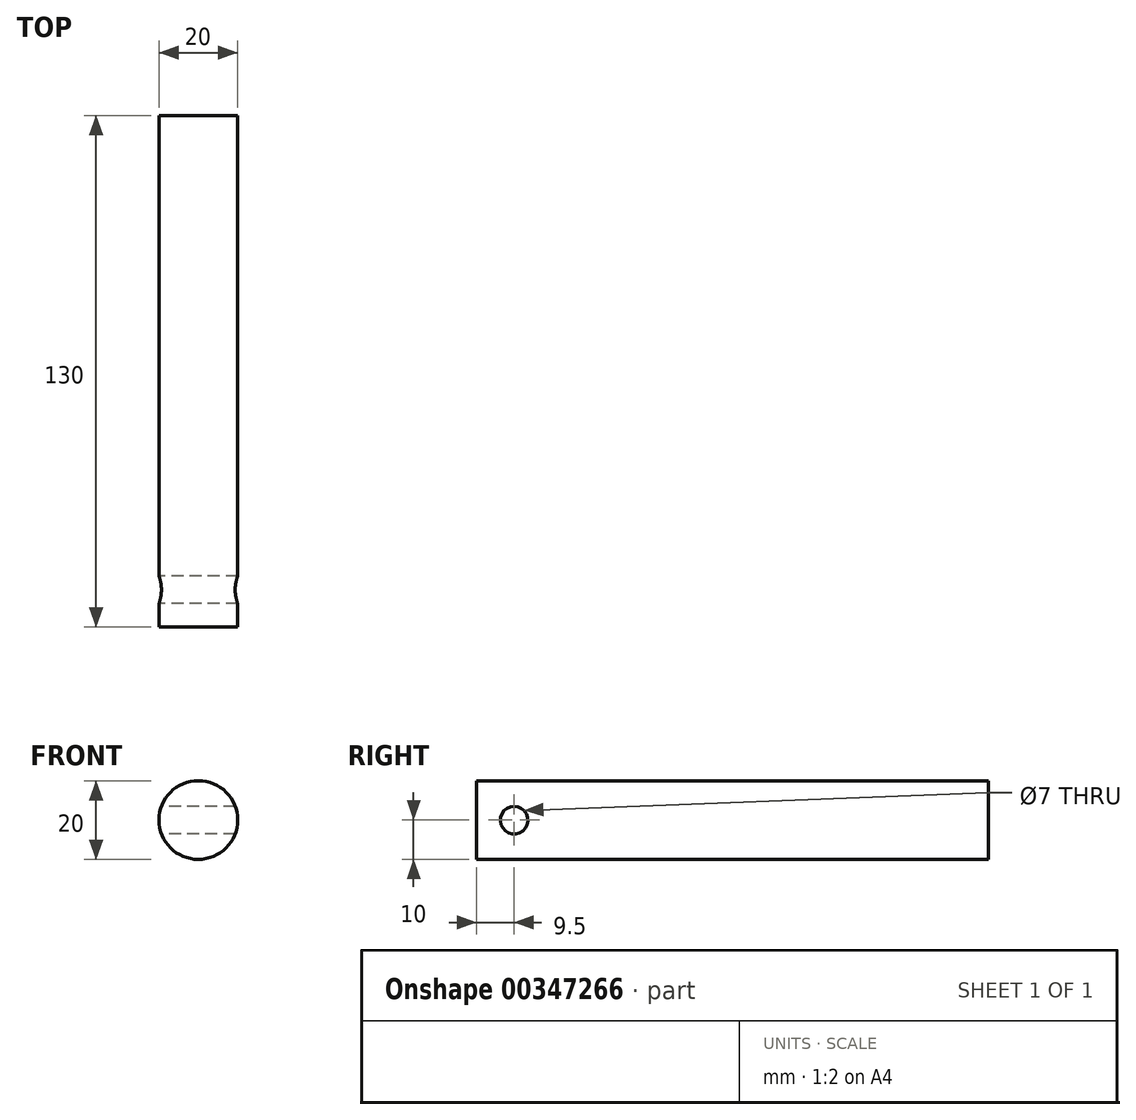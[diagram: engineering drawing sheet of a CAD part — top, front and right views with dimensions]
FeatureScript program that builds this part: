
annotation { "Feature Type Name" : "Feature", "Feature Type Description" : "" }
export const myFeature = defineFeature(function(context is Context, id is Id, definition is map)
    precondition{}
    {
        {
            var Q0;
            Q0=qCreatedBy(makeId("Front.planeOp"),FACE);
            var sketch = newSketch(context, id + "F0", { "sketchPlane" : qUnion([Q0])});
            skCircle(sketch, "E0", {"center": v(0, 0) * mm, "radius": 10 * mm});
            skSolve(sketch);
        }
        {
            var Q0;
            Q0=qCreatedBy(makeId("Right.planeOp"),FACE);
            var sketch = newSketch(context, id + "F1", { "sketchPlane" : qUnion([Q0])});
            skLineSegment(sketch, "E1.bottom", {"start": v(0, -10) * mm, "end": v(-130, -10) * mm});
            skLineSegment(sketch, "E1.top", {"start": v(0, 10) * mm, "end": v(-130, 10) * mm});
            skLineSegment(sketch, "E1.left", {"start": v(0, -10) * mm, "end": v(0, 10) * mm});
            skLineSegment(sketch, "E1.right", {"start": v(-130, -10) * mm, "end": v(-130, 10) * mm});
            skCircle(sketch, "E2", {"center": v(-120.5, 0) * mm, "radius": 3.5 * mm});
            skSolve(sketch);
        }
        {
            var Q0;
            Q0=makeQuery(id+"F1.imprint","IMPRINT",FACE,{"disambiguationData":[TD([[makeQuery(id+"F1.imprint","IMPRINT",EDGE,{"derivedFrom":sQuery(id+"F1.wireOp",EDGE,"E1.bottom")}),-1.0]])]});
            extrude(context, id + "F2", {"entities" : qUnion([Q0]), "depth" : 25 * mm, "symmetric" : true});
        }
        {
            var Q0;
            Q0 = qSketchRegion(id + "F0", true);
            extrude(context, id + "F3", {"entities" : qUnion([Q0]), "operationType" : NewBodyOperationType.INTERSECT, "depth" : 149 * mm});
        }
    });
